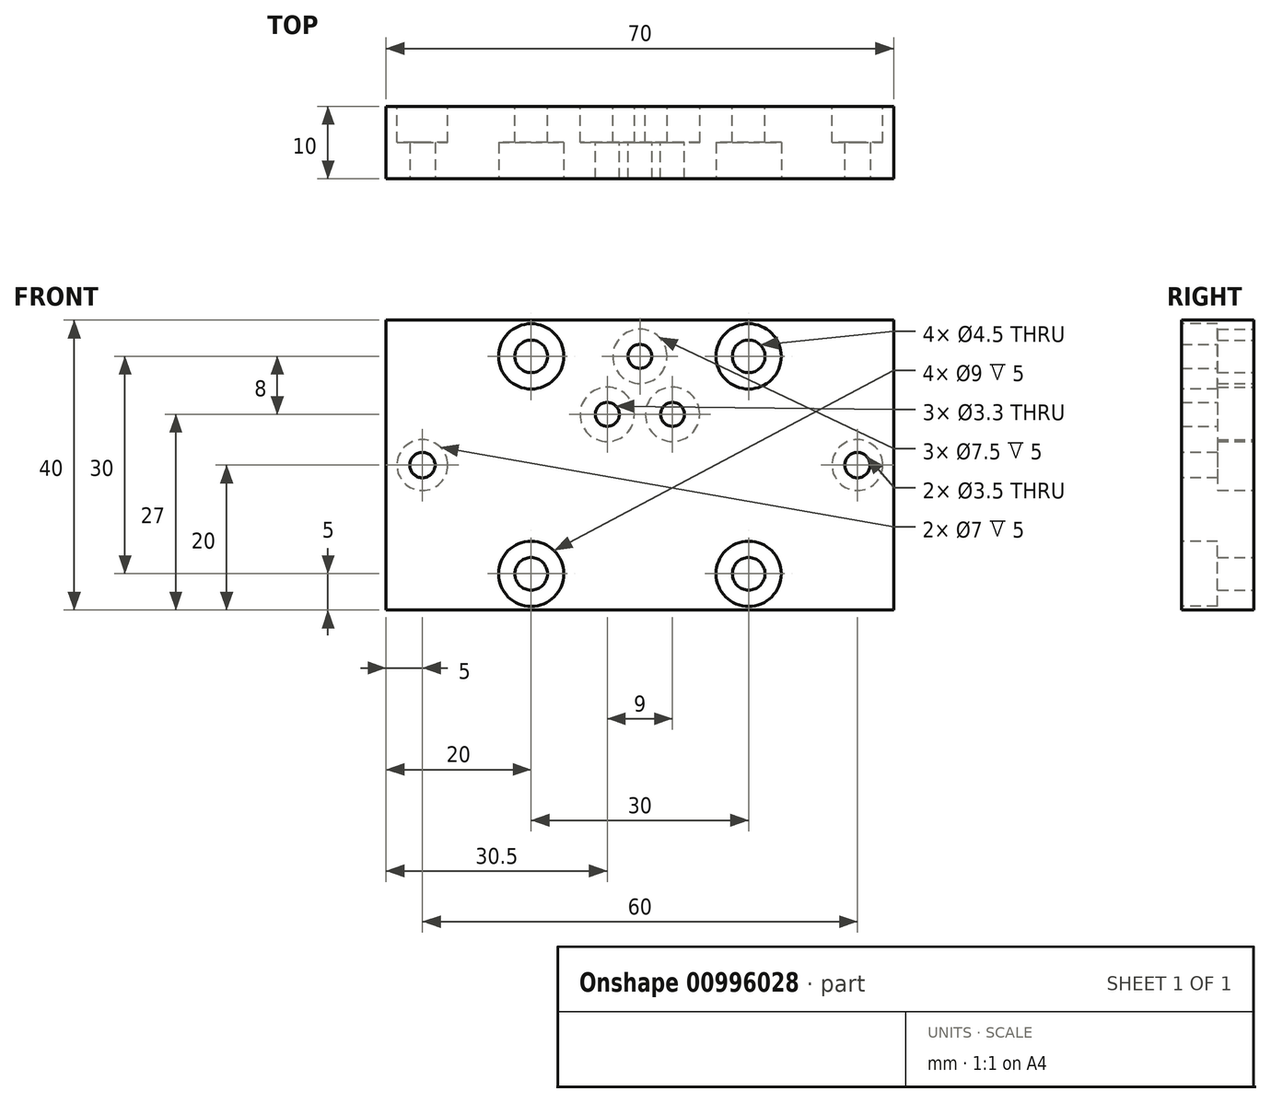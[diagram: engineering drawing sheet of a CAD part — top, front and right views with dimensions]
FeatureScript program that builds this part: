
annotation { "Feature Type Name" : "Feature", "Feature Type Description" : "" }
export const myFeature = defineFeature(function(context is Context, id is Id, definition is map)
    precondition{}
    {
        {
            var Q0;
            Q0=qCreatedBy(makeId("Front.planeOp"),FACE);
            var sketch = newSketch(context, id + "F0", { "sketchPlane" : qUnion([Q0])});
            skLineSegment(sketch, "E0.bottom", {"start": v(-70, 20) * mm, "end": v(0, 20) * mm});
            skLineSegment(sketch, "E0.top", {"start": v(-70, -20) * mm, "end": v(0, -20) * mm});
            skLineSegment(sketch, "E0.left", {"start": v(-70, 20) * mm, "end": v(-70, -20) * mm});
            skLineSegment(sketch, "E0.right", {"start": v(0, 20) * mm, "end": v(0, -20) * mm});
            skLineSegment(sketch, "E1.bottom", {"start": v(-50, 15) * mm, "end": v(-20, 15) * mm, "construction": true});
            skLineSegment(sketch, "E1.top", {"start": v(-50, -15) * mm, "end": v(-20, -15) * mm, "construction": true});
            skLineSegment(sketch, "E1.left", {"start": v(-50, 15) * mm, "end": v(-50, -15) * mm, "construction": true});
            skLineSegment(sketch, "E1.right", {"start": v(-20, 15) * mm, "end": v(-20, -15) * mm, "construction": true});
            skPoint(sketch, "E2", {"position": v(-35, 20) * mm});
            skPoint(sketch, "E3", {"position": v(-35, 15) * mm});
            skPoint(sketch, "E4", {"position": v(-20, 0) * mm});
            skPoint(sketch, "E5", {"position": v(0, 0) * mm});
            skCircle(sketch, "E6", {"center": v(-50, 15) * mm, "radius": 2.25 * mm});
            skCircle(sketch, "E7", {"center": v(-20, 15) * mm, "radius": 2.25 * mm});
            skCircle(sketch, "E8", {"center": v(-20, -15) * mm, "radius": 2.25 * mm});
            skCircle(sketch, "E9", {"center": v(-50, -15) * mm, "radius": 2.25 * mm});
            skCircle(sketch, "E10", {"center": v(-35, 15) * mm, "radius": 1.65 * mm});
            skCircle(sketch, "E11", {"center": v(-30.5, 7) * mm, "radius": 1.65 * mm});
            skCircle(sketch, "E12", {"center": v(-39.5, 7) * mm, "radius": 1.65 * mm});
            skSolve(sketch);
        }
        {
            var Q0;
            Q0=makeQuery(id+"F0.imprint","IMPRINT",FACE,{"disambiguationData":[TD([[makeQuery(id+"F0.imprint","IMPRINT",EDGE,{"derivedFrom":sQuery(id+"F0.wireOp",EDGE,"E0.bottom")}),-1.0]])]});
            extrude(context, id + "F1", {"entities" : qUnion([Q0]), "depth" : 10 * mm, "offsetDistance" : 25 * mm});
        }
        {
            var Q0;
            Q0=makeQuery(id+"F1.opExtrude","CAP_FACE",FACE,{"disambiguationData":[OSD([sQuery(id+"F0.wireOp",EDGE,"E0.bottom"),sQuery(id+"F0.wireOp",EDGE,"E0.top"),sQuery(id+"F0.wireOp",EDGE,"E0.left"),sQuery(id+"F0.wireOp",EDGE,"E0.right"),sQuery(id+"F0.wireOp",EDGE,"E6"),sQuery(id+"F0.wireOp",EDGE,"E7"),sQuery(id+"F0.wireOp",EDGE,"E8"),sQuery(id+"F0.wireOp",EDGE,"E9"),sQuery(id+"F0.wireOp",EDGE,"E10"),sQuery(id+"F0.wireOp",EDGE,"E11"),sQuery(id+"F0.wireOp",EDGE,"E12")])],"isStart":false});
            var sketch = newSketch(context, id + "F2", { "sketchPlane" : qUnion([Q0])});
            skCircle(sketch, "E13", {"center": v(-50, 15) * mm, "radius": 4.5 * mm});
            skCircle(sketch, "E14", {"center": v(-20, 15) * mm, "radius": 4.5 * mm});
            skCircle(sketch, "E15", {"center": v(-20, -15) * mm, "radius": 4.5 * mm});
            skCircle(sketch, "E16", {"center": v(-50, -15) * mm, "radius": 4.5 * mm});
            skSolve(sketch);
        }
        {
            var Q0;
            Q0=makeQuery(id+"F2.imprint","IMPRINT",FACE,{"disambiguationData":[TD([[makeQuery(id+"F2.imprint","IMPRINT",EDGE,{"derivedFrom":makeQuery(id+"F1.opExtrude","CAP_EDGE",EDGE,{"disambiguationData":[OSD([sQuery(id+"F0.wireOp",EDGE,"E6")])],"isStart":false})}),1.0]])]});
            var Q1;
            Q1=makeQuery(id+"F2.imprint","IMPRINT",FACE,{"disambiguationData":[TD([[makeQuery(id+"F2.imprint","IMPRINT",EDGE,{"derivedFrom":makeQuery(id+"F1.opExtrude","CAP_EDGE",EDGE,{"disambiguationData":[OSD([sQuery(id+"F0.wireOp",EDGE,"E7")])],"isStart":false})}),1.0]])]});
            var Q2;
            Q2=makeQuery(id+"F2.imprint","IMPRINT",FACE,{"disambiguationData":[TD([[makeQuery(id+"F2.imprint","IMPRINT",EDGE,{"derivedFrom":makeQuery(id+"F1.opExtrude","CAP_EDGE",EDGE,{"disambiguationData":[OSD([sQuery(id+"F0.wireOp",EDGE,"E8")])],"isStart":false})}),1.0]])]});
            var Q3;
            Q3=makeQuery(id+"F2.imprint","IMPRINT",FACE,{"disambiguationData":[TD([[makeQuery(id+"F2.imprint","IMPRINT",EDGE,{"derivedFrom":makeQuery(id+"F1.opExtrude","CAP_EDGE",EDGE,{"disambiguationData":[OSD([sQuery(id+"F0.wireOp",EDGE,"E9")])],"isStart":false})}),1.0]])]});
            var Q4;
            Q4=makeQuery(id+"F2.imprint","IMPRINT",FACE,{"disambiguationData":[TD([[makeQuery(id+"F2.imprint","IMPRINT",EDGE,{"derivedFrom":sQuery(id+"F2.wireOp",EDGE,"E14")}),1.0]])]});
            var Q5;
            Q5=makeQuery(id+"F2.imprint","IMPRINT",FACE,{"disambiguationData":[TD([[makeQuery(id+"F2.imprint","IMPRINT",EDGE,{"derivedFrom":sQuery(id+"F2.wireOp",EDGE,"E15")}),1.0]])]});
            var Q6;
            Q6=makeQuery(id+"F2.imprint","IMPRINT",FACE,{"disambiguationData":[TD([[makeQuery(id+"F2.imprint","IMPRINT",EDGE,{"derivedFrom":sQuery(id+"F2.wireOp",EDGE,"E16")}),1.0]])]});
            var Q7;
            Q7=makeQuery(id+"F2.imprint","IMPRINT",FACE,{"disambiguationData":[TD([[makeQuery(id+"F2.imprint","IMPRINT",EDGE,{"derivedFrom":sQuery(id+"F2.wireOp",EDGE,"E13")}),1.0]])]});
            extrude(context, id + "F3", {"entities" : qUnion([Q0, Q1, Q2, Q3, Q4, Q5, Q6, Q7]), "operationType" : NewBodyOperationType.REMOVE, "oppositeDirection" : true, "depth" : 5 * mm, "offsetDistance" : 25 * mm});
        }
        {
            var Q0;
            Q0=makeQuery(id+"F1.opExtrude","CAP_FACE",FACE,{"disambiguationData":[OSD([sQuery(id+"F0.wireOp",EDGE,"E0.bottom"),sQuery(id+"F0.wireOp",EDGE,"E0.top"),sQuery(id+"F0.wireOp",EDGE,"E0.left"),sQuery(id+"F0.wireOp",EDGE,"E0.right"),sQuery(id+"F0.wireOp",EDGE,"E6"),sQuery(id+"F0.wireOp",EDGE,"E7"),sQuery(id+"F0.wireOp",EDGE,"E8"),sQuery(id+"F0.wireOp",EDGE,"E9"),sQuery(id+"F0.wireOp",EDGE,"E10"),sQuery(id+"F0.wireOp",EDGE,"E11"),sQuery(id+"F0.wireOp",EDGE,"E12")])],"isStart":true});
            var sketch = newSketch(context, id + "F4", { "sketchPlane" : qUnion([Q0])});
            skCircle(sketch, "E17", {"center": v(35, 15) * mm, "radius": 3.75 * mm});
            skCircle(sketch, "E18", {"center": v(30.5, 7) * mm, "radius": 3.75 * mm});
            skCircle(sketch, "E19", {"center": v(39.5, 7) * mm, "radius": 3.75 * mm});
            skSolve(sketch);
        }
        {
            var Q0;
            Q0 = qSketchRegion(id + "F4", true);
            extrude(context, id + "F5", {"entities" : qUnion([Q0]), "operationType" : NewBodyOperationType.REMOVE, "oppositeDirection" : true, "depth" : 5 * mm, "offsetDistance" : 25 * mm});
        }
        {
            var Q0;
            Q0=makeQuery(id+"F1.opExtrude","CAP_FACE",FACE,{"disambiguationData":[OSD([sQuery(id+"F0.wireOp",EDGE,"E0.bottom"),sQuery(id+"F0.wireOp",EDGE,"E0.top"),sQuery(id+"F0.wireOp",EDGE,"E0.left"),sQuery(id+"F0.wireOp",EDGE,"E0.right"),sQuery(id+"F0.wireOp",EDGE,"E6"),sQuery(id+"F0.wireOp",EDGE,"E7"),sQuery(id+"F0.wireOp",EDGE,"E8"),sQuery(id+"F0.wireOp",EDGE,"E9"),sQuery(id+"F0.wireOp",EDGE,"E10"),sQuery(id+"F0.wireOp",EDGE,"E11"),sQuery(id+"F0.wireOp",EDGE,"E12")])],"isStart":false});
            var sketch = newSketch(context, id + "F6", { "sketchPlane" : qUnion([Q0])});
            skCircle(sketch, "E20", {"center": v(-65, 0) * mm, "radius": 1.75 * mm});
            skCircle(sketch, "E21", {"center": v(-5, 0) * mm, "radius": 1.75 * mm});
            skSolve(sketch);
        }
        {
            var Q0;
            Q0 = qSketchRegion(id + "F6", true);
            extrude(context, id + "F7", {"entities" : qUnion([Q0]), "operationType" : NewBodyOperationType.REMOVE, "oppositeDirection" : true, "depth" : 25 * mm, "offsetDistance" : 25 * mm});
        }
        {
            var Q0;
            Q0=makeQuery(id+"F1.opExtrude","CAP_FACE",FACE,{"disambiguationData":[OSD([sQuery(id+"F0.wireOp",EDGE,"E0.bottom"),sQuery(id+"F0.wireOp",EDGE,"E0.top"),sQuery(id+"F0.wireOp",EDGE,"E0.left"),sQuery(id+"F0.wireOp",EDGE,"E0.right"),sQuery(id+"F0.wireOp",EDGE,"E6"),sQuery(id+"F0.wireOp",EDGE,"E7"),sQuery(id+"F0.wireOp",EDGE,"E8"),sQuery(id+"F0.wireOp",EDGE,"E9"),sQuery(id+"F0.wireOp",EDGE,"E10"),sQuery(id+"F0.wireOp",EDGE,"E11"),sQuery(id+"F0.wireOp",EDGE,"E12")])],"isStart":true});
            var sketch = newSketch(context, id + "F8", { "sketchPlane" : qUnion([Q0])});
            skCircle(sketch, "E22", {"center": v(5, 0) * mm, "radius": 3.5 * mm});
            skCircle(sketch, "E23", {"center": v(65, 0) * mm, "radius": 3.5 * mm});
            skSolve(sketch);
        }
        {
            var Q0;
            Q0 = qSketchRegion(id + "F8", true);
            extrude(context, id + "F9", {"entities" : qUnion([Q0]), "operationType" : NewBodyOperationType.REMOVE, "oppositeDirection" : true, "depth" : 5 * mm, "offsetDistance" : 25 * mm});
        }
    });
